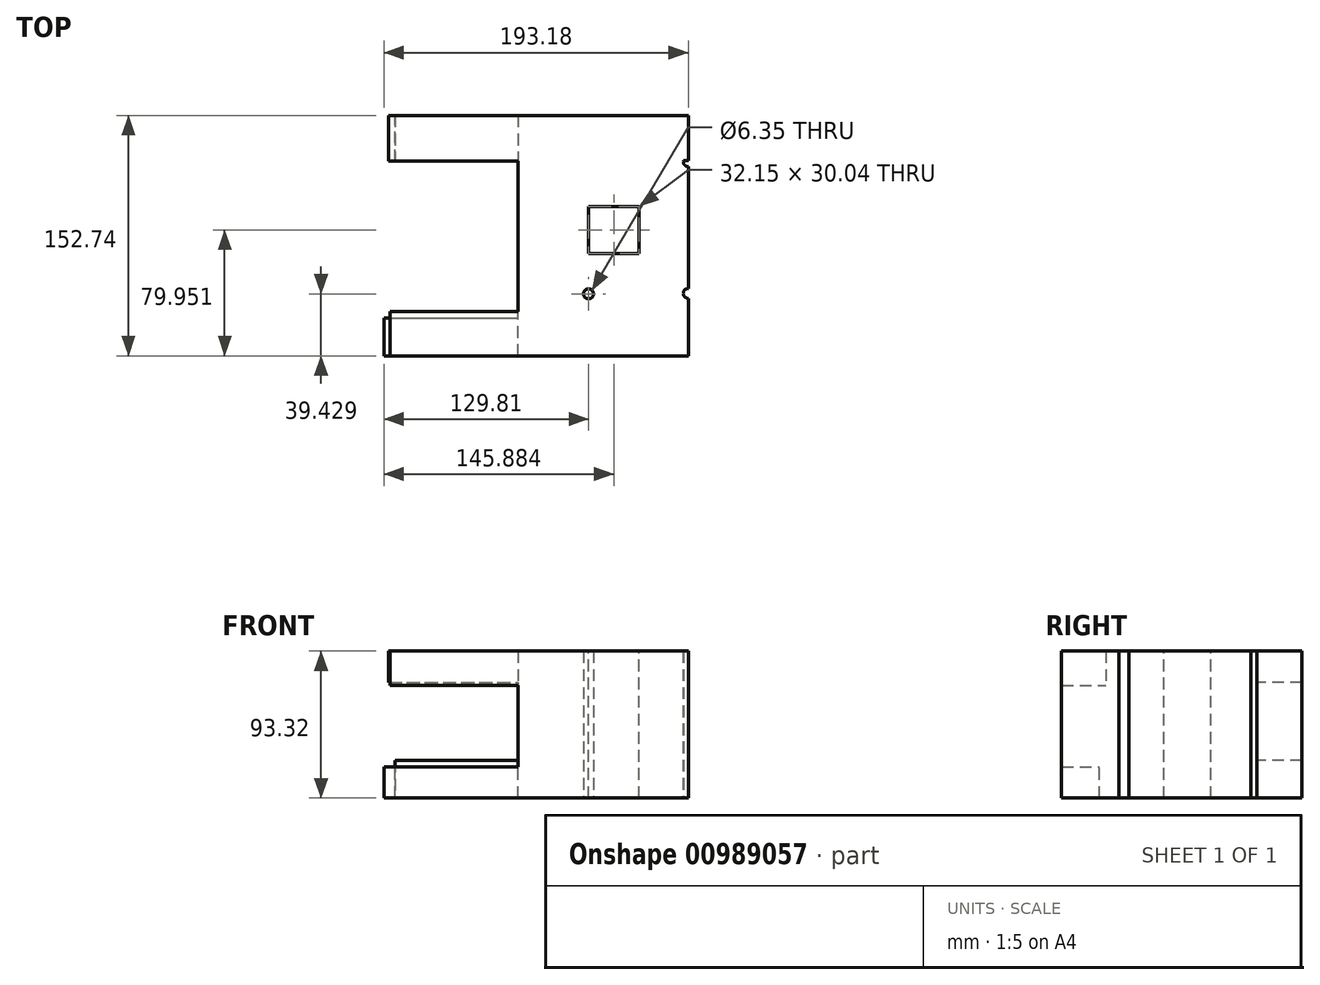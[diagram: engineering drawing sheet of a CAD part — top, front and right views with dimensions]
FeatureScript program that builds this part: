
annotation { "Feature Type Name" : "Feature", "Feature Type Description" : "" }
export const myFeature = defineFeature(function(context is Context, id is Id, definition is map)
    precondition{}
    {
        {
            var Q0;
            Q0=qCreatedBy(makeId("Front.planeOp"),FACE);
            var sketch = newSketch(context, id + "F0", { "sketchPlane" : qUnion([Q0])});
            skLineSegment(sketch, "E0.bottom", {"start": v(-44.8, 54.39) * mm, "end": v(63.37, 54.39) * mm});
            skLineSegment(sketch, "E0.top", {"start": v(-44.8, -38.93) * mm, "end": v(63.37, -38.93) * mm});
            skLineSegment(sketch, "E0.left", {"start": v(-44.8, 54.39) * mm, "end": v(-44.8, -38.93) * mm});
            skLineSegment(sketch, "E0.right", {"start": v(63.37, 54.39) * mm, "end": v(63.37, -38.93) * mm});
            skSolve(sketch);
        }
        {
            var Q0;
            Q0=makeQuery(id+"F0.imprint","IMPRINT",FACE,{"disambiguationData":[TD([[makeQuery(id+"F0.imprint","IMPRINT",EDGE,{"derivedFrom":sQuery(id+"F0.wireOp",EDGE,"E0.bottom")}),-1.0]])]});
            extrude(context, id + "F1", {"entities" : qUnion([Q0]), "depth" : 152.74 * mm, "offsetDistance" : 25.4 * mm});
        }
        {
            var Q0;
            Q0=makeQuery(id+"F1.opExtrude","SWEPT_FACE",FACE,{"disambiguationData":[OSD([sQuery(id+"F0.wireOp",EDGE,"E0.left")])]});
            var sketch = newSketch(context, id + "F2", { "sketchPlane" : qUnion([Q0])});
            skLineSegment(sketch, "E1.bottom", {"start": v(152.74, 54.39) * mm, "end": v(124.52, 54.39) * mm});
            skLineSegment(sketch, "E1.top", {"start": v(152.74, 32.7) * mm, "end": v(124.52, 32.7) * mm});
            skLineSegment(sketch, "E1.left", {"start": v(152.74, 54.39) * mm, "end": v(152.74, 32.7) * mm});
            skLineSegment(sketch, "E1.right", {"start": v(124.52, 54.39) * mm, "end": v(124.52, 32.7) * mm});
            skSolve(sketch);
        }
        {
            var Q0;
            Q0=makeQuery(id+"F2.imprint","IMPRINT",FACE,{"disambiguationData":[TD([[makeQuery(id+"F2.imprint","IMPRINT",EDGE,{"derivedFrom":sQuery(id+"F2.wireOp",EDGE,"E1.bottom")}),1.0]])]});
            extrude(context, id + "F3", {"entities" : qUnion([Q0]), "operationType" : NewBodyOperationType.ADD, "depth" : 81.18 * mm, "offsetDistance" : 25.4 * mm});
        }
        {
            var Q0;
            Q0=makeQuery(id+"F1.opExtrude","SWEPT_FACE",FACE,{"disambiguationData":[OSD([sQuery(id+"F0.wireOp",EDGE,"E0.left")])]});
            var sketch = newSketch(context, id + "F4", { "sketchPlane" : qUnion([Q0])});
            skLineSegment(sketch, "E2.bottom", {"start": v(0, 54.39) * mm, "end": v(29.06, 54.39) * mm});
            skLineSegment(sketch, "E2.top", {"start": v(0, 34.42) * mm, "end": v(29.06, 34.42) * mm});
            skLineSegment(sketch, "E2.left", {"start": v(0, 54.39) * mm, "end": v(0, 34.42) * mm});
            skLineSegment(sketch, "E2.right", {"start": v(29.06, 54.39) * mm, "end": v(29.06, 34.42) * mm});
            skSolve(sketch);
        }
        {
            var Q0;
            Q0=makeQuery(id+"F4.imprint","IMPRINT",FACE,{"disambiguationData":[TD([[makeQuery(id+"F4.imprint","IMPRINT",EDGE,{"derivedFrom":sQuery(id+"F4.wireOp",EDGE,"E2.bottom")}),1.0]])]});
            extrude(context, id + "F5", {"entities" : qUnion([Q0]), "operationType" : NewBodyOperationType.ADD, "depth" : 82.15 * mm, "offsetDistance" : 25.4 * mm});
        }
        {
            var Q0;
            Q0=makeQuery(id+"F1.opExtrude","SWEPT_FACE",FACE,{"disambiguationData":[OSD([sQuery(id+"F0.wireOp",EDGE,"E0.left")])]});
            var sketch = newSketch(context, id + "F6", { "sketchPlane" : qUnion([Q0])});
            skLineSegment(sketch, "E3.bottom", {"start": v(152.74, -38.93) * mm, "end": v(128.76, -38.93) * mm});
            skLineSegment(sketch, "E3.top", {"start": v(152.74, -19.21) * mm, "end": v(128.76, -19.21) * mm});
            skLineSegment(sketch, "E3.left", {"start": v(152.74, -38.93) * mm, "end": v(152.74, -19.21) * mm});
            skLineSegment(sketch, "E3.right", {"start": v(128.76, -38.93) * mm, "end": v(128.76, -19.21) * mm});
            skSolve(sketch);
        }
        {
            var Q0;
            Q0 = qSketchRegion(id + "F6", true);
            var Q1;
            Q1=makeQuery(id+"F6.imprint","IMPRINT",FACE,{"disambiguationData":[TD([[makeQuery(id+"F6.imprint","IMPRINT",EDGE,{"derivedFrom":sQuery(id+"F6.wireOp",EDGE,"E3.bottom")}),-1.0]])]});
            extrude(context, id + "F7", {"entities" : qUnion([Q0, Q1]), "operationType" : NewBodyOperationType.ADD, "depth" : 85 * mm, "offsetDistance" : 25.4 * mm});
        }
        {
            var Q0;
            Q0=makeQuery(id+"F1.opExtrude","SWEPT_FACE",FACE,{"disambiguationData":[OSD([sQuery(id+"F0.wireOp",EDGE,"E0.left")])]});
            var sketch = newSketch(context, id + "F8", { "sketchPlane" : qUnion([Q0])});
            skLineSegment(sketch, "E4.bottom", {"start": v(0, -38.93) * mm, "end": v(29.08, -38.93) * mm});
            skLineSegment(sketch, "E4.top", {"start": v(0, -15.12) * mm, "end": v(29.08, -15.12) * mm});
            skLineSegment(sketch, "E4.left", {"start": v(0, -38.93) * mm, "end": v(0, -15.12) * mm});
            skLineSegment(sketch, "E4.right", {"start": v(29.08, -38.93) * mm, "end": v(29.08, -15.12) * mm});
            skSolve(sketch);
        }
        {
            var Q0;
            Q0=makeQuery(id+"F8.imprint","IMPRINT",FACE,{"disambiguationData":[TD([[makeQuery(id+"F8.imprint","IMPRINT",EDGE,{"derivedFrom":sQuery(id+"F8.wireOp",EDGE,"E4.bottom")}),-1.0]])]});
            extrude(context, id + "F9", {"entities" : qUnion([Q0]), "operationType" : NewBodyOperationType.ADD, "depth" : 78.15 * mm, "offsetDistance" : 25.4 * mm});
        }
        {
            var Q0;
            Q0=makeQuery(id+"F9.boolean.opBoolean","MERGE",FACE,{"derivedFrom":[makeQuery(id+"F7.boolean.opBoolean","MERGE",FACE,{"derivedFrom":[makeQuery(id+"F1.opExtrude","SWEPT_FACE",FACE,{"disambiguationData":[OSD([sQuery(id+"F0.wireOp",EDGE,"E0.top")])]}),makeQuery(id+"F7.opExtrude","SWEPT_FACE",FACE,{"disambiguationData":[OSD([sQuery(id+"F6.wireOp",EDGE,"E3.bottom")])]})]}),makeQuery(id+"F9.opExtrude","SWEPT_FACE",FACE,{"disambiguationData":[OSD([sQuery(id+"F8.wireOp",EDGE,"E4.bottom")])]})]});
            var sketch = newSketch(context, id + "F10", { "sketchPlane" : qUnion([Q0])});
            skLineSegment(sketch, "E5", {"start": v(26.86, 152.74) * mm, "end": v(63.37, 113.02) * mm});
            skLineSegment(sketch, "E6", {"start": v(63.37, 113.02) * mm, "end": v(45.11, 132.88) * mm});
            skSolve(sketch);
        }
        {
            var Q0;
            Q0=sQuery(id+"F10.wireOp",VERTEX,"E5.end");
            var Q1;
            Q1=makeQuery(id+"F1.opExtrude","SWEPT_BODY",BODY,{"disambiguationData":[OSD([sQuery(id+"F0.wireOp",EDGE,"E0.bottom"),sQuery(id+"F0.wireOp",EDGE,"E0.top"),sQuery(id+"F0.wireOp",EDGE,"E0.left"),sQuery(id+"F0.wireOp",EDGE,"E0.right")])]});
            hole(context, id + "F11", {"style" : HoleStyle.SIMPLE, "endStyle" : HoleEndStyle.THROUGH, "holeDiameter" : 6.35 * mm, "majorDiameter" : 6.35 * mm, "isTappedThrough" : true, "tappedDepth" : 12.7 * mm, "tapClearance" : 3, "locations" : qUnion([Q0]), "scope" : qUnion([Q1])});
        }
        {
            var Q0;
            Q0=makeQuery(id+"F9.boolean.opBoolean","MERGE",FACE,{"derivedFrom":[makeQuery(id+"F7.boolean.opBoolean","MERGE",FACE,{"derivedFrom":[makeQuery(id+"F1.opExtrude","SWEPT_FACE",FACE,{"disambiguationData":[OSD([sQuery(id+"F0.wireOp",EDGE,"E0.top")])]}),makeQuery(id+"F7.opExtrude","SWEPT_FACE",FACE,{"disambiguationData":[OSD([sQuery(id+"F6.wireOp",EDGE,"E3.bottom")])]})]}),makeQuery(id+"F9.opExtrude","SWEPT_FACE",FACE,{"disambiguationData":[OSD([sQuery(id+"F8.wireOp",EDGE,"E4.bottom")])]})]});
            var sketch = newSketch(context, id + "F12", { "sketchPlane" : qUnion([Q0])});
            skPoint(sketch, "E7", {"position": v(63.37, 29.28) * mm});
            skSolve(sketch);
        }
        {
            var Q0;
            Q0=sQuery(id+"F12.wireOp",VERTEX,"E7");
            var Q1;
            Q1=makeQuery(id+"F1.opExtrude","SWEPT_BODY",BODY,{"disambiguationData":[OSD([sQuery(id+"F0.wireOp",EDGE,"E0.bottom"),sQuery(id+"F0.wireOp",EDGE,"E0.top"),sQuery(id+"F0.wireOp",EDGE,"E0.left"),sQuery(id+"F0.wireOp",EDGE,"E0.right")])]});
            hole(context, id + "F13", {"style" : HoleStyle.SIMPLE, "endStyle" : HoleEndStyle.THROUGH, "holeDiameter" : 6.35 * mm, "majorDiameter" : 6.35 * mm, "isTappedThrough" : true, "tappedDepth" : 12.7 * mm, "tapClearance" : 3, "locations" : qUnion([Q0]), "scope" : qUnion([Q1])});
        }
        {
            var Q0;
            Q0 = qSketchRegion(id + "F0", true);
            var Q1;
            Q1=makeQuery(id+"F9.boolean.opBoolean","MERGE",FACE,{"derivedFrom":[makeQuery(id+"F5.boolean.opBoolean","MERGE",FACE,{"derivedFrom":[makeQuery(id+"F1.opExtrude","CAP_FACE",FACE,{"disambiguationData":[OSD([sQuery(id+"F0.wireOp",EDGE,"E0.bottom"),sQuery(id+"F0.wireOp",EDGE,"E0.top"),sQuery(id+"F0.wireOp",EDGE,"E0.left"),sQuery(id+"F0.wireOp",EDGE,"E0.right")])],"isStart":true}),makeQuery(id+"F5.opExtrude","SWEPT_FACE",FACE,{"disambiguationData":[OSD([sQuery(id+"F4.wireOp",EDGE,"E2.left")])]})]}),makeQuery(id+"F9.opExtrude","SWEPT_FACE",FACE,{"disambiguationData":[OSD([sQuery(id+"F8.wireOp",EDGE,"E4.left")])]})]});
            extrude(context, id + "F14", {"entities" : qUnion([Q0, Q1]), "operationType" : NewBodyOperationType.ADD, "depth" : 28.77 * mm, "offsetDistance" : 25.4 * mm});
        }
        {
            var Q0;
            {var subQ0=sQuery(id+"F8.wireOp",EDGE,"E4.bottom");var subQ1=sQuery(id+"F0.wireOp",EDGE,"E0.top");Q0=makeQuery(id+"F14.boolean.opBoolean","MERGE",FACE,{"derivedFrom":[makeQuery(id+"F9.boolean.opBoolean","MERGE",FACE,{"derivedFrom":[makeQuery(id+"F7.boolean.opBoolean","MERGE",FACE,{"derivedFrom":[makeQuery(id+"F1.opExtrude","SWEPT_FACE",FACE,{"disambiguationData":[OSD([subQ1])]}),makeQuery(id+"F7.opExtrude","SWEPT_FACE",FACE,{"disambiguationData":[OSD([sQuery(id+"F6.wireOp",EDGE,"E3.bottom")])]})]}),makeQuery(id+"F9.opExtrude","SWEPT_FACE",FACE,{"disambiguationData":[OSD([subQ0])]})]}),makeQuery(id+"F14.opExtrude","SWEPT_FACE",FACE,{"disambiguationData":[OSD([subQ1])]}),makeQuery(id+"F14.opExtrude","SWEPT_FACE",FACE,{"disambiguationData":[OSD([subQ1,subQ0,sQuery(id+"F8.wireOp",EDGE,"E4.left")])]})]});}
            var sketch = newSketch(context, id + "F15", { "sketchPlane" : qUnion([Q0])});
            skCircle(sketch, "E8", {"center": v(0, 113.31) * mm, "radius": 34.1 * mm});
            skSolve(sketch);
        }
        {
            var Q0;
            Q0=sQuery(id+"F15.wireOp",VERTEX,"E8.center");
            var Q1;
            Q1=makeQuery(id+"F1.opExtrude","SWEPT_BODY",BODY,{"disambiguationData":[OSD([sQuery(id+"F0.wireOp",EDGE,"E0.bottom"),sQuery(id+"F0.wireOp",EDGE,"E0.top"),sQuery(id+"F0.wireOp",EDGE,"E0.left"),sQuery(id+"F0.wireOp",EDGE,"E0.right")])]});
            hole(context, id + "F16", {"style" : HoleStyle.SIMPLE, "endStyle" : HoleEndStyle.THROUGH, "holeDiameter" : 6.35 * mm, "majorDiameter" : 6.35 * mm, "isTappedThrough" : true, "tappedDepth" : 12.7 * mm, "tapClearance" : 3, "locations" : qUnion([Q0]), "scope" : qUnion([Q1])});
        }
        {
            var Q0;
            {var subQ0=sQuery(id+"F4.wireOp",EDGE,"E2.bottom");var subQ1=sQuery(id+"F0.wireOp",EDGE,"E0.bottom");Q0=makeQuery(id+"F14.boolean.opBoolean","MERGE",FACE,{"derivedFrom":[makeQuery(id+"F5.boolean.opBoolean","MERGE",FACE,{"derivedFrom":[makeQuery(id+"F3.boolean.opBoolean","MERGE",FACE,{"derivedFrom":[makeQuery(id+"F1.opExtrude","SWEPT_FACE",FACE,{"disambiguationData":[OSD([subQ1])]}),makeQuery(id+"F3.opExtrude","SWEPT_FACE",FACE,{"disambiguationData":[OSD([sQuery(id+"F2.wireOp",EDGE,"E1.bottom")])]})]}),makeQuery(id+"F5.opExtrude","SWEPT_FACE",FACE,{"disambiguationData":[OSD([subQ0])]})]}),makeQuery(id+"F14.opExtrude","SWEPT_FACE",FACE,{"disambiguationData":[OSD([subQ1])]}),makeQuery(id+"F14.opExtrude","SWEPT_FACE",FACE,{"disambiguationData":[OSD([subQ1,subQ0,sQuery(id+"F4.wireOp",EDGE,"E2.left")])]})]});}
            var sketch = newSketch(context, id + "F17", { "sketchPlane" : qUnion([Q0])});
            skLineSegment(sketch, "E9.bottom", {"start": v(32.15, -57.77) * mm, "end": v(0, -57.77) * mm});
            skLineSegment(sketch, "E9.top", {"start": v(32.15, -87.8) * mm, "end": v(0, -87.8) * mm});
            skLineSegment(sketch, "E9.left", {"start": v(32.15, -57.77) * mm, "end": v(32.15, -87.8) * mm});
            skLineSegment(sketch, "E9.right", {"start": v(0, -57.77) * mm, "end": v(0, -87.8) * mm});
            skSolve(sketch);
        }
        {
            var Q0;
            Q0 = qSketchRegion(id + "F17", true);
            var Q1;
            Q1=makeQuery(id+"F17.imprint","IMPRINT",FACE,{"disambiguationData":[TD([[makeQuery(id+"F17.imprint","IMPRINT",EDGE,{"derivedFrom":sQuery(id+"F17.wireOp",EDGE,"E9.bottom")}),1.0]])]});
            extrude(context, id + "F18", {"entities" : qUnion([Q0, Q1]), "operationType" : NewBodyOperationType.REMOVE, "oppositeDirection" : true, "depth" : 95.81 * mm, "offsetDistance" : 25.4 * mm});
        }
    });
